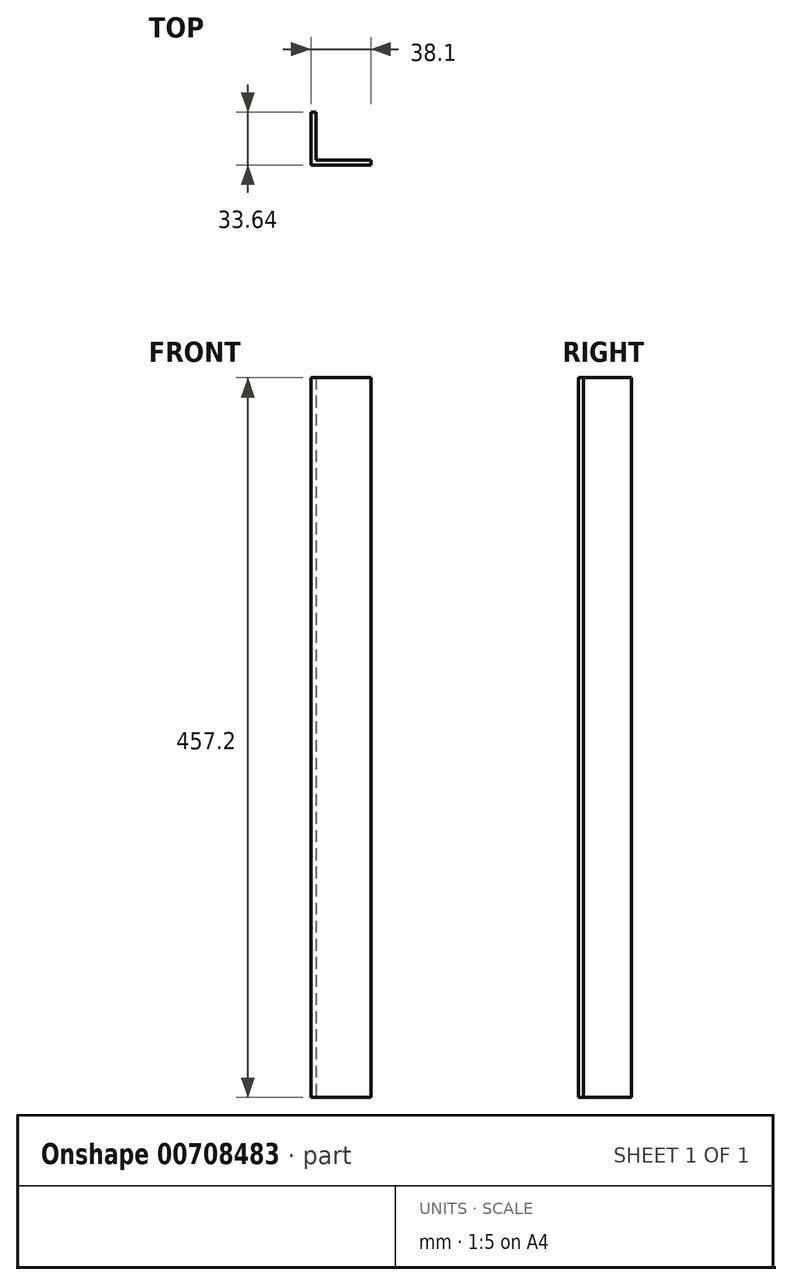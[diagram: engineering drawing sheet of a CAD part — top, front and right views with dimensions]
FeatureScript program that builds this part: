
annotation { "Feature Type Name" : "Feature", "Feature Type Description" : "" }
export const myFeature = defineFeature(function(context is Context, id is Id, definition is map)
    precondition{}
    {
        {
            var Q0;
            Q0=qCreatedBy(makeId("Top.planeOp"),FACE);
            var sketch = newSketch(context, id + "F0", { "sketchPlane" : qUnion([Q0])});
            skLineSegment(sketch, "E0", {"start": v(0, 0) * mm, "end": v(38.1, 0) * mm});
            skLineSegment(sketch, "E1", {"start": v(0, 0) * mm, "end": v(0, 33.64) * mm});
            skLineSegment(sketch, "E2.0", {"start": v(3.18, 3.18) * mm, "end": v(3.18, 33.64) * mm});
            skLineSegment(sketch, "E2.1", {"start": v(3.18, 3.18) * mm, "end": v(38.1, 3.18) * mm});
            skLineSegment(sketch, "E3", {"start": v(0, 33.64) * mm, "end": v(3.18, 33.64) * mm});
            skLineSegment(sketch, "E4", {"start": v(38.1, 3.18) * mm, "end": v(38.1, 0) * mm});
            skSolve(sketch);
        }
        {
            var Q0;
            Q0 = qSketchRegion(id + "F0", true);
            extrude(context, id + "F1", {"entities" : qUnion([Q0]), "depth" : 457.2 * mm, "offsetDistance" : 25.4 * mm});
        }
    });
